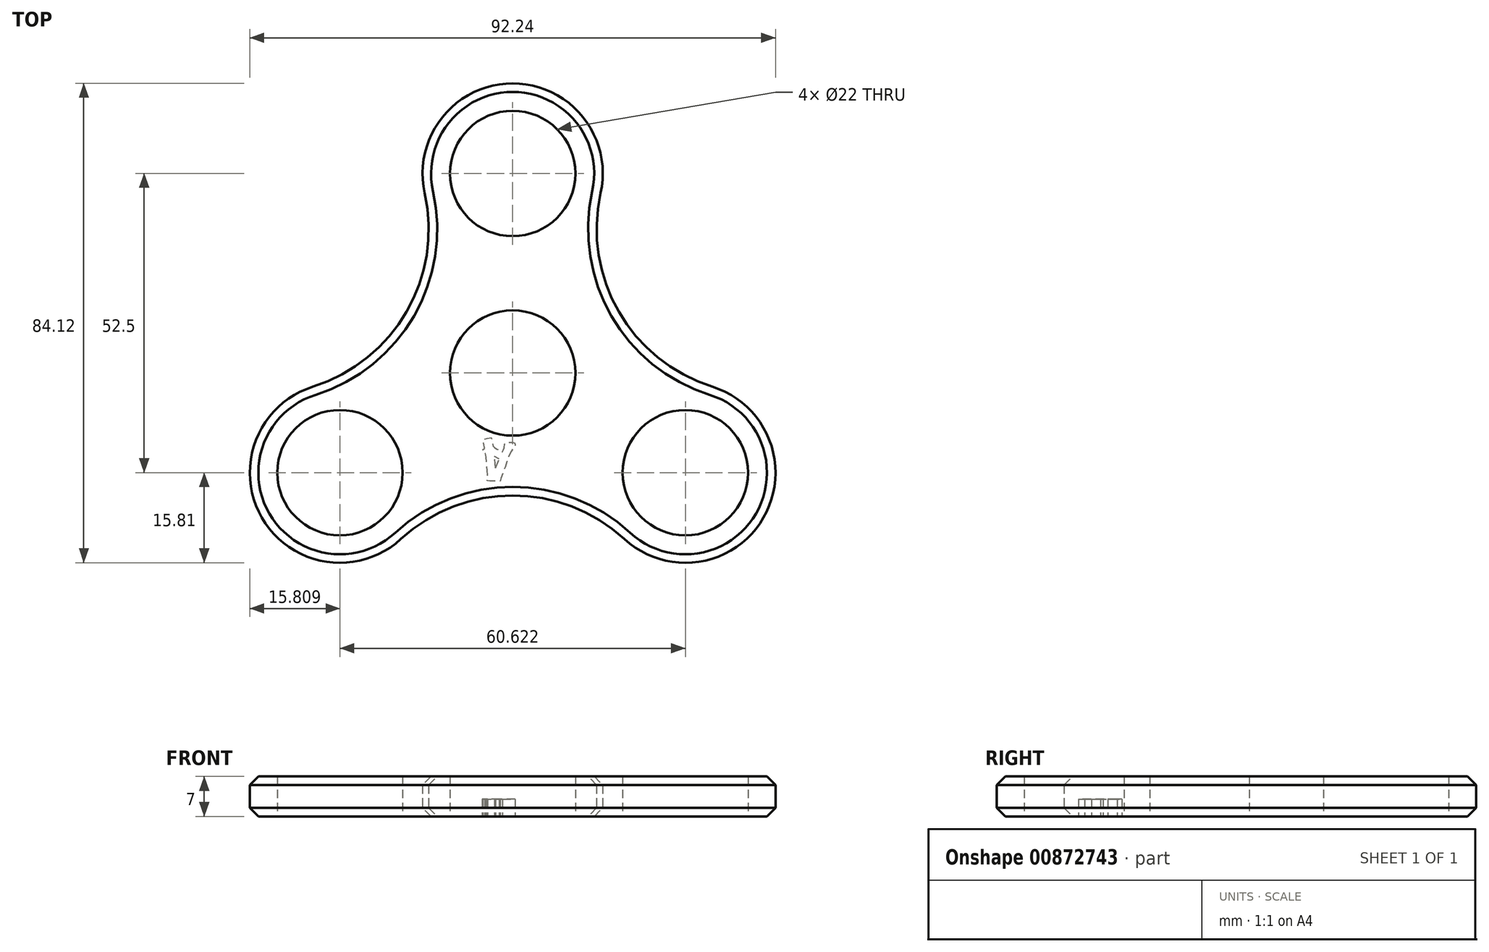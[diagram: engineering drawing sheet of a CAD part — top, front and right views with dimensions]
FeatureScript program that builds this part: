
annotation { "Feature Type Name" : "Feature", "Feature Type Description" : "" }
export const myFeature = defineFeature(function(context is Context, id is Id, definition is map)
    precondition{}
    {
        {
            var Q0;
            Q0=qCreatedBy(makeId("Top.planeOp"),FACE);
            var sketch = newSketch(context, id + "F0", { "sketchPlane" : qUnion([Q0])});
            skCircle(sketch, "E0", {"center": v(0, 0) * mm, "radius": 11 * mm});
            skLineSegment(sketch, "E1", {"start": v(0, 0) * mm, "end": v(0, 35) * mm, "construction": true});
            skArc(sketch, "E2", {"start": v(15.43, 31.56) * mm, "mid": v(0, 50.81) * mm, "end": v(-15.43, 31.56) * mm});
            skArc(sketch, "E3.1.0", {"start": v(-35.04, -2.41) * mm, "mid": v(-44, -25.4) * mm, "end": v(-19.61, -29.14) * mm});
            skArc(sketch, "E3.2.0", {"start": v(19.61, -29.14) * mm, "mid": v(44, -25.4) * mm, "end": v(35.04, -2.41) * mm});
            skArc(sketch, "E4", {"start": v(0, -21.5) * mm, "mid": v(-10.52, -23.48) * mm, "end": v(-19.61, -29.14) * mm});
            skArc(sketch, "E5", {"start": v(19.61, -29.14) * mm, "mid": v(10.52, -23.48) * mm, "end": v(0, -21.5) * mm});
            skArc(sketch, "E6.1.0", {"start": v(18.62, 10.75) * mm, "mid": v(25.6, 2.62) * mm, "end": v(35.04, -2.41) * mm});
            skArc(sketch, "E6.1.1", {"start": v(15.43, 31.56) * mm, "mid": v(15.07, 20.85) * mm, "end": v(18.62, 10.75) * mm});
            skArc(sketch, "E6.2.0", {"start": v(-18.62, 10.75) * mm, "mid": v(-15.07, 20.85) * mm, "end": v(-15.43, 31.56) * mm});
            skArc(sketch, "E6.2.1", {"start": v(-35.04, -2.41) * mm, "mid": v(-25.6, 2.62) * mm, "end": v(-18.62, 10.75) * mm});
            skCircle(sketch, "E7", {"center": v(0, 35) * mm, "radius": 11 * mm});
            skCircle(sketch, "E8.1.0", {"center": v(-30.31, -17.5) * mm, "radius": 11 * mm});
            skCircle(sketch, "E8.2.0", {"center": v(30.31, -17.5) * mm, "radius": 11 * mm});
            skCircle(sketch, "E9.cCircle", {"center": v(0, 17.5) * mm, "radius": 4.9 * mm, "construction": true});
            skLineSegment(sketch, "E9.0", {"start": v(2.83, 22.4) * mm, "end": v(5.66, 17.5) * mm});
            skLineSegment(sketch, "E9.1", {"start": v(5.66, 17.5) * mm, "end": v(2.83, 12.6) * mm});
            skLineSegment(sketch, "E9.2", {"start": v(2.83, 12.6) * mm, "end": v(-2.83, 12.6) * mm});
            skLineSegment(sketch, "E9.3", {"start": v(-2.83, 12.6) * mm, "end": v(-5.66, 17.5) * mm});
            skLineSegment(sketch, "E9.4", {"start": v(-5.66, 17.5) * mm, "end": v(-2.83, 22.4) * mm});
            skLineSegment(sketch, "E9.5", {"start": v(-2.83, 22.4) * mm, "end": v(2.83, 22.4) * mm});
            skLineSegment(sketch, "E10.1.0", {"start": v(-9.5, -8.75) * mm, "end": v(-12.33, -13.65) * mm});
            skLineSegment(sketch, "E10.1.1", {"start": v(-12.33, -13.65) * mm, "end": v(-17.98, -13.65) * mm});
            skLineSegment(sketch, "E10.1.2", {"start": v(-17.98, -13.65) * mm, "end": v(-20.81, -8.75) * mm});
            skLineSegment(sketch, "E10.1.3", {"start": v(-20.81, -8.75) * mm, "end": v(-17.98, -3.85) * mm});
            skLineSegment(sketch, "E10.1.4", {"start": v(-17.98, -3.85) * mm, "end": v(-12.33, -3.85) * mm});
            skLineSegment(sketch, "E10.1.5", {"start": v(-12.33, -3.85) * mm, "end": v(-9.5, -8.75) * mm});
            skLineSegment(sketch, "E10.2.0", {"start": v(12.33, -3.85) * mm, "end": v(17.98, -3.85) * mm});
            skLineSegment(sketch, "E10.2.1", {"start": v(17.98, -3.85) * mm, "end": v(20.81, -8.75) * mm});
            skLineSegment(sketch, "E10.2.2", {"start": v(20.81, -8.75) * mm, "end": v(17.98, -13.65) * mm});
            skLineSegment(sketch, "E10.2.3", {"start": v(17.98, -13.65) * mm, "end": v(12.33, -13.65) * mm});
            skLineSegment(sketch, "E10.2.4", {"start": v(12.33, -13.65) * mm, "end": v(9.5, -8.75) * mm});
            skLineSegment(sketch, "E10.2.5", {"start": v(9.5, -8.75) * mm, "end": v(12.33, -3.85) * mm});
            skLineSegment(sketch, "E11", {"start": v(0, 0) * mm, "end": v(-18.62, 10.75) * mm, "construction": true});
            skCircle(sketch, "E12.cCircle", {"center": v(-14.07, 8.13) * mm, "radius": 4 * mm, "construction": true});
            skLineSegment(sketch, "E12.0", {"start": v(-11.76, 12.13) * mm, "end": v(-9.45, 8.13) * mm});
            skLineSegment(sketch, "E12.1", {"start": v(-9.45, 8.13) * mm, "end": v(-11.76, 4.13) * mm});
            skLineSegment(sketch, "E12.2", {"start": v(-11.76, 4.13) * mm, "end": v(-16.38, 4.13) * mm});
            skLineSegment(sketch, "E12.3", {"start": v(-16.38, 4.13) * mm, "end": v(-18.7, 8.13) * mm});
            skLineSegment(sketch, "E12.4", {"start": v(-18.7, 8.12) * mm, "end": v(-16.38, 12.13) * mm});
            skLineSegment(sketch, "E12.5", {"start": v(-16.38, 12.13) * mm, "end": v(-11.76, 12.13) * mm});
            skPoint(sketch, "E12.0.midPoint", {"position": v(-10.6, 10.13) * mm});
            skLineSegment(sketch, "E13.1.0", {"start": v(2.3, -20.25) * mm, "end": v(-2.3, -20.25) * mm});
            skLineSegment(sketch, "E13.1.1", {"start": v(-2.3, -20.25) * mm, "end": v(-4.62, -16.25) * mm});
            skLineSegment(sketch, "E13.1.2", {"start": v(-4.62, -16.25) * mm, "end": v(-2.3, -12.25) * mm});
            skLineSegment(sketch, "E13.1.3", {"start": v(-2.3, -12.25) * mm, "end": v(2.3, -12.25) * mm});
            skLineSegment(sketch, "E13.1.4", {"start": v(2.3, -12.25) * mm, "end": v(4.62, -16.25) * mm});
            skLineSegment(sketch, "E13.1.5", {"start": v(4.62, -16.25) * mm, "end": v(2.3, -20.25) * mm});
            skLineSegment(sketch, "E13.2.0", {"start": v(16.38, 12.12) * mm, "end": v(18.7, 8.12) * mm});
            skLineSegment(sketch, "E13.2.1", {"start": v(18.7, 8.12) * mm, "end": v(16.38, 4.12) * mm});
            skLineSegment(sketch, "E13.2.2", {"start": v(16.38, 4.12) * mm, "end": v(11.76, 4.12) * mm});
            skLineSegment(sketch, "E13.2.3", {"start": v(11.76, 4.12) * mm, "end": v(9.45, 8.12) * mm});
            skLineSegment(sketch, "E13.2.4", {"start": v(9.45, 8.12) * mm, "end": v(11.76, 12.12) * mm});
            skLineSegment(sketch, "E13.2.5", {"start": v(11.76, 12.12) * mm, "end": v(16.38, 12.12) * mm});
            skSolve(sketch);
        }
        {
            var Q0;
            Q0=makeQuery(id+"F0.imprint","IMPRINT",FACE,{"disambiguationData":[TD([[makeQuery(id+"F0.imprint","IMPRINT",EDGE,{"derivedFrom":sQuery(id+"F0.wireOp",EDGE,"E3.1.0")}),1.0]])]});
            var Q1;
            Q1=makeQuery(id+"F0.imprint","IMPRINT",FACE,{"disambiguationData":[TD([[makeQuery(id+"F0.imprint","IMPRINT",EDGE,{"derivedFrom":sQuery(id+"F0.wireOp",EDGE,"E2")}),1.0]])]});
            var Q2;
            Q2=makeQuery(id+"F0.imprint","IMPRINT",FACE,{"disambiguationData":[TD([[makeQuery(id+"F0.imprint","IMPRINT",EDGE,{"derivedFrom":sQuery(id+"F0.wireOp",EDGE,"E3.2.0")}),1.0]])]});
            var Q3;
            Q3=makeQuery(id+"F0.imprint","IMPRINT",FACE,{"disambiguationData":[TD([[makeQuery(id+"F0.imprint","IMPRINT",EDGE,{"derivedFrom":sQuery(id+"F0.wireOp",EDGE,"E0")}),-1.0]])]});
            var Q4;
            Q4=makeQuery(id+"F0.imprint","IMPRINT",FACE,{"disambiguationData":[TD([[makeQuery(id+"F0.imprint","IMPRINT",EDGE,{"derivedFrom":sQuery(id+"F0.wireOp",EDGE,"E9.0")}),-1.0]])]});
            var Q5;
            Q5=makeQuery(id+"F0.imprint","IMPRINT",FACE,{"disambiguationData":[TD([[makeQuery(id+"F0.imprint","IMPRINT",EDGE,{"derivedFrom":sQuery(id+"F0.wireOp",EDGE,"E10.1.0")}),-1.0]])]});
            var Q6;
            Q6=makeQuery(id+"F0.imprint","IMPRINT",FACE,{"disambiguationData":[TD([[makeQuery(id+"F0.imprint","IMPRINT",EDGE,{"derivedFrom":sQuery(id+"F0.wireOp",EDGE,"E10.2.0")}),-1.0]])]});
            var Q7;
            Q7=makeQuery(id+"F0.imprint","IMPRINT",FACE,{"disambiguationData":[TD([[makeQuery(id+"F0.imprint","IMPRINT",EDGE,{"derivedFrom":sQuery(id+"F0.wireOp",EDGE,"E13.2.0")}),-1.0]])]});
            var Q8;
            Q8=makeQuery(id+"F0.imprint","IMPRINT",FACE,{"disambiguationData":[TD([[makeQuery(id+"F0.imprint","IMPRINT",EDGE,{"derivedFrom":sQuery(id+"F0.wireOp",EDGE,"E13.1.0")}),-1.0]])]});
            var Q9;
            Q9=makeQuery(id+"F0.imprint","IMPRINT",FACE,{"disambiguationData":[TD([[makeQuery(id+"F0.imprint","IMPRINT",EDGE,{"derivedFrom":sQuery(id+"F0.wireOp",EDGE,"E12.0")}),-1.0]])]});
            extrude(context, id + "F1", {"entities" : qUnion([Q0, Q1, Q2, Q3, Q4, Q5, Q6, Q7, Q8, Q9]), "depth" : 7 * mm, "offsetDistance" : 25 * mm});
        }
        {
            var Q0;
            Q0=makeQuery(id+"F1.opExtrude","CAP_EDGE",EDGE,{"disambiguationData":[OSD([sQuery(id+"F0.wireOp",EDGE,"E6.2.1")])],"isStart":true});
            var Q1;
            Q1=makeQuery(id+"F1.opExtrude","CAP_EDGE",EDGE,{"disambiguationData":[OSD([sQuery(id+"F0.wireOp",EDGE,"E6.2.0")])],"isStart":true});
            var Q2;
            Q2=makeQuery(id+"F1.opExtrude","CAP_EDGE",EDGE,{"disambiguationData":[OSD([sQuery(id+"F0.wireOp",EDGE,"E2")])],"isStart":true});
            var Q3;
            Q3=makeQuery(id+"F1.opExtrude","CAP_EDGE",EDGE,{"disambiguationData":[OSD([sQuery(id+"F0.wireOp",EDGE,"E6.1.1")])],"isStart":true});
            var Q4;
            Q4=makeQuery(id+"F1.opExtrude","CAP_EDGE",EDGE,{"disambiguationData":[OSD([sQuery(id+"F0.wireOp",EDGE,"E6.1.0")])],"isStart":true});
            var Q5;
            Q5=makeQuery(id+"F1.opExtrude","CAP_EDGE",EDGE,{"disambiguationData":[OSD([sQuery(id+"F0.wireOp",EDGE,"E3.2.0")])],"isStart":true});
            var Q6;
            Q6=makeQuery(id+"F1.opExtrude","CAP_EDGE",EDGE,{"disambiguationData":[OSD([sQuery(id+"F0.wireOp",EDGE,"E5")])],"isStart":true});
            var Q7;
            Q7=makeQuery(id+"F1.opExtrude","CAP_EDGE",EDGE,{"disambiguationData":[OSD([sQuery(id+"F0.wireOp",EDGE,"E4")])],"isStart":true});
            var Q8;
            Q8=makeQuery(id+"F1.opExtrude","CAP_EDGE",EDGE,{"disambiguationData":[OSD([sQuery(id+"F0.wireOp",EDGE,"E3.1.0")])],"isStart":true});
            var Q9;
            Q9=makeQuery(id+"F1.opExtrude","CAP_EDGE",EDGE,{"disambiguationData":[OSD([sQuery(id+"F0.wireOp",EDGE,"E2")])],"isStart":false});
            var Q10;
            Q10=makeQuery(id+"F1.opExtrude","CAP_EDGE",EDGE,{"disambiguationData":[OSD([sQuery(id+"F0.wireOp",EDGE,"E6.2.0")])],"isStart":false});
            var Q11;
            Q11=makeQuery(id+"F1.opExtrude","CAP_EDGE",EDGE,{"disambiguationData":[OSD([sQuery(id+"F0.wireOp",EDGE,"E6.2.1")])],"isStart":false});
            var Q12;
            Q12=makeQuery(id+"F1.opExtrude","CAP_EDGE",EDGE,{"disambiguationData":[OSD([sQuery(id+"F0.wireOp",EDGE,"E3.1.0")])],"isStart":false});
            var Q13;
            Q13=makeQuery(id+"F1.opExtrude","CAP_EDGE",EDGE,{"disambiguationData":[OSD([sQuery(id+"F0.wireOp",EDGE,"E5")])],"isStart":false});
            var Q14;
            Q14=makeQuery(id+"F1.opExtrude","CAP_EDGE",EDGE,{"disambiguationData":[OSD([sQuery(id+"F0.wireOp",EDGE,"E4")])],"isStart":false});
            var Q15;
            Q15=makeQuery(id+"F1.opExtrude","CAP_EDGE",EDGE,{"disambiguationData":[OSD([sQuery(id+"F0.wireOp",EDGE,"E3.2.0")])],"isStart":false});
            var Q16;
            Q16=makeQuery(id+"F1.opExtrude","CAP_EDGE",EDGE,{"disambiguationData":[OSD([sQuery(id+"F0.wireOp",EDGE,"E6.1.0")])],"isStart":false});
            var Q17;
            Q17=makeQuery(id+"F1.opExtrude","CAP_EDGE",EDGE,{"disambiguationData":[OSD([sQuery(id+"F0.wireOp",EDGE,"E6.1.1")])],"isStart":false});
            chamfer(context, id + "F2", {"entities" : qUnion([Q0, Q1, Q2, Q3, Q4, Q5, Q6, Q7, Q8, Q9, Q10, Q11, Q12, Q13, Q14, Q15, Q16, Q17]), "width" : 1.5 * mm, "tangentPropagation" : true});
        }
        {
            var Q0;
            Q0=makeQuery(id+"F1.opExtrude","CAP_FACE",FACE,{"disambiguationData":[OSD([sQuery(id+"F0.wireOp",EDGE,"E0"),sQuery(id+"F0.wireOp",EDGE,"E2"),sQuery(id+"F0.wireOp",EDGE,"E3.1.0"),sQuery(id+"F0.wireOp",EDGE,"E3.2.0"),sQuery(id+"F0.wireOp",EDGE,"E4"),sQuery(id+"F0.wireOp",EDGE,"E5"),sQuery(id+"F0.wireOp",EDGE,"E6.1.0"),sQuery(id+"F0.wireOp",EDGE,"E6.1.1"),sQuery(id+"F0.wireOp",EDGE,"E6.2.0"),sQuery(id+"F0.wireOp",EDGE,"E6.2.1"),sQuery(id+"F0.wireOp",EDGE,"E7"),sQuery(id+"F0.wireOp",EDGE,"E8.1.0"),sQuery(id+"F0.wireOp",EDGE,"E8.2.0")])],"isStart":true});
            var sketch = newSketch(context, id + "F3", { "sketchPlane" : qUnion([Q0])});
            skFitSpline(sketch, "E14", {"points": [v(15.47, 11.75) * mm, v(15.3, 11.71) * mm, v(15.13, 11.7) * mm, v(15, 11.62) * mm, v(13.64, 10.78) * mm, v(12.3, 9.92) * mm, v(10.95, 9.1) * mm, v(10.42, 8.77) * mm, v(9.83, 8.53) * mm, v(9.28, 8.23) * mm, v(9.17, 8.16) * mm, v(9.04, 7.95) * mm, v(9.07, 7.84) * mm, v(9.18, 7.4) * mm, v(9.3, 6.95) * mm, v(9.49, 6.52) * mm, v(9.64, 6.17) * mm, v(9.9, 6.15) * mm, v(10.2, 6.42) * mm, v(10.32, 6.55) * mm, v(10.4, 6.74) * mm, v(10.54, 6.83) * mm, v(11.24, 7.29) * mm, v(11.96, 7.72) * mm, v(12.67, 8.16) * mm]});
            skFitSpline(sketch, "E15", {"points": [v(12.67, 8.16) * mm, v(12.69, 8.14) * mm, v(12.7, 8.13) * mm, v(12.72, 8.11) * mm]});
            skFitSpline(sketch, "E16", {"points": [v(12.72, 8.11) * mm, v(12.74, 8.1) * mm, v(12.76, 8.08) * mm, v(12.77, 8.07) * mm]});
            skFitSpline(sketch, "E17", {"points": [v(12.77, 8.07) * mm, v(12.12, 7.22) * mm, v(11.46, 6.37) * mm, v(10.81, 5.52) * mm, v(10.72, 5.4) * mm, v(10.56, 5.22) * mm, v(10.6, 5.12) * mm, v(10.78, 4.55) * mm, v(11, 3.98) * mm, v(11.25, 3.45) * mm, v(11.4, 3.15) * mm, v(11.67, 3.2) * mm, v(11.94, 3.36) * mm, v(13.17, 4.15) * mm, v(14.4, 4.95) * mm, v(15.65, 5.71) * mm]});
            skFitSpline(sketch, "E18", {"points": [v(15.65, 5.71) * mm, v(16.44, 6.2) * mm, v(17.26, 6.62) * mm, v(18.06, 7.09) * mm, v(18.15, 7.14) * mm, v(18.24, 7.35) * mm, v(18.2, 7.43) * mm, v(18.05, 7.81) * mm, v(17.88, 8.2) * mm, v(17.65, 8.55) * mm, v(17.47, 8.8) * mm, v(17.24, 8.78) * mm, v(16.93, 8.57) * mm, v(15.92, 7.88) * mm, v(14.86, 7.24) * mm, v(13.82, 6.58) * mm]});
            skFitSpline(sketch, "E19", {"points": [v(13.82, 6.58) * mm, v(13.8, 6.62) * mm, v(13.76, 6.65) * mm, v(13.74, 6.68) * mm]});
            skFitSpline(sketch, "E20", {"points": [v(13.74, 6.68) * mm, v(14.3, 7.34) * mm, v(14.88, 7.98) * mm, v(15.42, 8.65) * mm, v(16.46, 9.95) * mm, v(16.63, 9.94) * mm, v(15.81, 11.51) * mm]});
            skFitSpline(sketch, "E21", {"points": [v(2.9, -16.8) * mm, v(2.9, -17.17) * mm, v(2.9, -17.54) * mm, v(2.88, -17.92) * mm, v(2.85, -18.56) * mm, v(2.85, -18.57) * mm, v(3.5, -18.75) * mm, v(3.56, -18.76) * mm, v(3.63, -18.78) * mm, v(3.7, -18.8) * mm]});
            skFitSpline(sketch, "E22", {"points": [v(3.7, -18.8) * mm, v(4.31, -18.92) * mm, v(4.61, -18.66) * mm, v(4.54, -18.03) * mm, v(4.32, -16.04) * mm, v(4.08, -14.05) * mm, v(3.87, -12.06) * mm, v(3.83, -11.63) * mm, v(3.62, -11.46) * mm, v(3.25, -11.4) * mm, v(3.07, -11.36) * mm, v(2.89, -11.35) * mm, v(2.7, -11.36) * mm, v(2.21, -11.38) * mm, v(2.12, -11.58) * mm, v(2.25, -12.06) * mm, v(2.4, -12.6) * mm, v(2.46, -13.17) * mm, v(2.56, -13.73) * mm]});
            skFitSpline(sketch, "E23", {"points": [v(-1.83, 13.85) * mm, v(-1.7, 13.54) * mm, v(-1.55, 13.34) * mm, v(-1.5, 13.1) * mm, v(-1.36, 12.35) * mm, v(-0.84, 12.16) * mm, v(-0.17, 12.18) * mm, v(0.01, 12.19) * mm, v(0.34, 12.2) * mm, v(0.36, 12.29) * mm, v(0.42, 12.5) * mm, v(0.41, 12.78) * mm, v(0.3, 12.96) * mm, v(-0.6, 14.43) * mm, v(-1.17, 16.03) * mm, v(-1.73, 17.64) * mm, v(-2.2, 18.99) * mm, v(-2.19, 19) * mm, v(-3.64, 18.99) * mm, v(-3.8, 18.99) * mm, v(-3.95, 18.97) * mm, v(-4.1, 18.96) * mm, v(-4.42, 18.94) * mm, v(-4.52, 18.8) * mm, v(-4.44, 18.49) * mm, v(-4.39, 18.3) * mm, v(-4.4, 18.1) * mm, v(-4.4, 17.9) * mm]});
            skFitSpline(sketch, "E24", {"points": [v(-4.4, 17.9) * mm, v(-4.5, 16.76) * mm, v(-4.61, 15.63) * mm, v(-4.72, 14.5) * mm, v(-4.73, 14.38) * mm, v(-4.72, 14.23) * mm, v(-4.8, 14.17) * mm, v(-5.11, 13.89) * mm, v(-5.36, 13.61) * mm, v(-4.97, 13.2) * mm, v(-4.93, 13.16) * mm, v(-4.97, 13.03) * mm, v(-4.99, 12.95) * mm, v(-5.03, 12.7) * mm, v(-5.06, 12.45) * mm, v(-5.13, 12.2) * mm, v(-5.24, 11.82) * mm, v(-5.1, 11.65) * mm, v(-4.72, 11.56) * mm, v(-3.74, 11.33) * mm, v(-3.74, 11.33) * mm, v(-3.55, 12.29) * mm, v(-3.5, 12.56) * mm, v(-3.42, 12.9) * mm, v(-3.23, 13.06) * mm, v(-2.82, 13.37) * mm, v(-2.34, 13.57) * mm, v(-1.83, 13.85) * mm]});
            skFitSpline(sketch, "E25", {"points": [v(-16.86, 2.82) * mm, v(-16.78, 2.83) * mm, v(-16.72, 2.84) * mm, v(-16.67, 2.83) * mm, v(-15.35, 2.72) * mm, v(-14.03, 2.6) * mm, v(-12.71, 2.47) * mm, v(-12.55, 2.45) * mm, v(-12.39, 2.39) * mm, v(-12.24, 2.3) * mm, v(-11.98, 2.17) * mm, v(-11.8, 2.23) * mm, v(-11.7, 2.5) * mm, v(-11.57, 2.82) * mm, v(-11.48, 3.16) * mm, v(-11.37, 3.5) * mm, v(-11.25, 3.84) * mm, v(-11.42, 4.02) * mm, v(-11.74, 4.04) * mm, v(-12, 4.07) * mm, v(-12.27, 4) * mm, v(-12.53, 4.02) * mm, v(-13.98, 4.14) * mm, v(-15.42, 4.27) * mm, v(-16.87, 4.41) * mm, v(-16.97, 4.42) * mm, v(-17.13, 4.52) * mm, v(-17.14, 4.59) * mm, v(-17.18, 4.93) * mm, v(-17.22, 5.28) * mm, v(-17.18, 5.61) * mm]});
            skFitSpline(sketch, "E26", {"points": [v(-17.18, 5.61) * mm, v(-17.15, 5.93) * mm, v(-17.2, 6.12) * mm, v(-17.55, 6.12) * mm, v(-17.83, 6.12) * mm, v(-18.1, 6.1) * mm, v(-18.38, 6.05) * mm]});
            skFitSpline(sketch, "E27", {"points": [v(-18.38, 6.05) * mm, v(-18.73, 5.99) * mm, v(-18.83, 5.75) * mm, v(-18.77, 5.42) * mm, v(-18.68, 4.97) * mm, v(-18.58, 4.51) * mm, v(-18.5, 4.05) * mm, v(-18.4, 3.36) * mm, v(-18.3, 2.66) * mm, v(-18.18, 1.96) * mm, v(-18.14, 1.7) * mm, v(-18.06, 1.45) * mm, v(-18, 1.19) * mm]});
            skFitSpline(sketch, "E28", {"points": [v(-18, 1.19) * mm, v(-17.75, 1.26) * mm, v(-17.5, 1.33) * mm, v(-17.26, 1.41) * mm, v(-17.2, 1.43) * mm, v(-17.16, 1.47) * mm, v(-17.12, 1.5) * mm, v(-16.8, 1.69) * mm, v(-16.59, 1.9) * mm, v(-16.8, 2.32) * mm, v(-16.86, 2.46) * mm, v(-16.84, 2.64) * mm, v(-16.86, 2.82) * mm]});
            skFitSpline(sketch, "E29", {"points": [v(11.05, -4.16) * mm, v(11.05, -4.16) * mm, v(11.04, -4.16) * mm, v(11.04, -4.16) * mm]});
            skFitSpline(sketch, "E30", {"points": [v(11.04, -4.16) * mm, v(11.01, -4.2) * mm, v(10.98, -4.25) * mm, v(10.95, -4.3) * mm, v(10.57, -4.86) * mm, v(10.68, -5.06) * mm, v(11.38, -5.14) * mm, v(11.54, -5.16) * mm, v(11.7, -5.2) * mm, v(11.86, -5.26) * mm, v(13, -5.66) * mm, v(14.15, -6.05) * mm, v(15.28, -6.48) * mm, v(15.95, -6.73) * mm, v(16.58, -7.06) * mm, v(17.23, -7.34) * mm]});
            skFitSpline(sketch, "E31", {"points": [v(17.23, -7.34) * mm, v(17.34, -7.38) * mm, v(17.57, -7.36) * mm, v(17.6, -7.3) * mm, v(17.83, -6.91) * mm, v(18.03, -6.51) * mm, v(18.2, -6.1) * mm, v(18.22, -6.03) * mm, v(18.04, -5.82) * mm, v(17.92, -5.77) * mm, v(15.9, -5.04) * mm, v(13.88, -4.32) * mm, v(11.85, -3.62) * mm, v(11.71, -3.57) * mm, v(11.5, -3.63) * mm, v(11.37, -3.72) * mm, v(11.23, -3.82) * mm, v(11.15, -4) * mm, v(11.05, -4.16) * mm]});
            skFitSpline(sketch, "E32", {"points": [v(-15.12, -11.88) * mm, v(-14.92, -11.83) * mm, v(-14.74, -11.83) * mm, v(-14.62, -11.75) * mm, v(-12.97, -10.53) * mm, v(-11.33, -9.3) * mm, v(-9.67, -8.09) * mm, v(-9.15, -7.7) * mm, v(-9.12, -7.69) * mm, v(-9.36, -7.08) * mm]});
            skFitSpline(sketch, "E33", {"points": [v(-9.36, -7.08) * mm, v(-9.4, -6.96) * mm, v(-9.45, -6.84) * mm, v(-9.5, -6.73) * mm]});
            skFitSpline(sketch, "E34", {"points": [v(-9.5, -6.73) * mm, v(-9.73, -6.24) * mm, v(-10.02, -6.2) * mm, v(-10.37, -6.63) * mm]});
            skFitSpline(sketch, "E35", {"points": [v(-10.37, -6.63) * mm, v(-10.49, -6.77) * mm, v(-10.62, -6.9) * mm, v(-10.76, -7) * mm, v(-11.5, -7.55) * mm, v(-12.22, -8.1) * mm, v(-12.97, -8.62) * mm, v(-13.8, -9.2) * mm, v(-14.68, -9.74) * mm, v(-15.52, -10.32) * mm, v(-15.62, -10.38) * mm, v(-15.72, -10.59) * mm, v(-15.7, -10.68) * mm, v(-15.54, -11.07) * mm, v(-15.34, -11.43) * mm, v(-15.12, -11.88) * mm]});
            skFitSpline(sketch, "E36", {"points": [v(15.81, 11.51) * mm, v(16.63, 9.94) * mm, v(16.46, 9.95) * mm, v(15.42, 8.65) * mm, v(14.88, 7.98) * mm, v(14.3, 7.34) * mm, v(13.74, 6.68) * mm]});
            skFitSpline(sketch, "E37", {"points": [v(13.74, 6.68) * mm, v(13.76, 6.65) * mm, v(13.8, 6.62) * mm, v(13.82, 6.58) * mm]});
            skFitSpline(sketch, "E38", {"points": [v(13.82, 6.58) * mm, v(14.86, 7.24) * mm, v(15.92, 7.88) * mm, v(16.93, 8.57) * mm, v(17.24, 8.78) * mm, v(17.47, 8.8) * mm, v(17.65, 8.55) * mm, v(17.88, 8.2) * mm, v(18.05, 7.81) * mm, v(18.2, 7.43) * mm, v(18.24, 7.35) * mm, v(18.15, 7.14) * mm, v(18.06, 7.09) * mm, v(17.26, 6.62) * mm, v(16.44, 6.2) * mm, v(15.65, 5.71) * mm]});
            skFitSpline(sketch, "E39", {"points": [v(15.65, 5.71) * mm, v(14.4, 4.95) * mm, v(13.17, 4.15) * mm, v(11.94, 3.36) * mm, v(11.67, 3.2) * mm, v(11.4, 3.15) * mm, v(11.25, 3.45) * mm, v(11, 3.98) * mm, v(10.78, 4.55) * mm, v(10.6, 5.12) * mm, v(10.58, 5.17) * mm, v(10.6, 5.24) * mm, v(10.65, 5.3) * mm]});
            skFitSpline(sketch, "E40", {"points": [v(10.65, 5.3) * mm, v(10.7, 5.38) * mm, v(10.76, 5.46) * mm, v(10.81, 5.52) * mm, v(11.46, 6.37) * mm, v(12.12, 7.22) * mm, v(12.77, 8.07) * mm]});
            skFitSpline(sketch, "E41", {"points": [v(12.77, 8.07) * mm, v(12.74, 8.1) * mm, v(12.7, 8.13) * mm, v(12.67, 8.16) * mm]});
            skFitSpline(sketch, "E42", {"points": [v(12.67, 8.16) * mm, v(11.96, 7.72) * mm, v(11.24, 7.29) * mm, v(10.54, 6.83) * mm, v(10.4, 6.74) * mm, v(10.32, 6.55) * mm, v(10.2, 6.42) * mm, v(9.9, 6.15) * mm, v(9.64, 6.17) * mm, v(9.49, 6.52) * mm, v(9.3, 6.95) * mm, v(9.18, 7.4) * mm, v(9.07, 7.84) * mm, v(9.04, 7.95) * mm, v(9.17, 8.16) * mm, v(9.28, 8.23) * mm, v(9.83, 8.53) * mm, v(10.42, 8.77) * mm, v(10.95, 9.1) * mm, v(12.3, 9.92) * mm, v(13.64, 10.78) * mm, v(15, 11.62) * mm, v(15.13, 11.7) * mm, v(15.3, 11.71) * mm, v(15.47, 11.75) * mm]});
            skFitSpline(sketch, "E43", {"points": [v(15.47, 11.75) * mm, v(15.58, 11.67) * mm, v(15.7, 11.6) * mm, v(15.81, 11.51) * mm]});
            skFitSpline(sketch, "E44", {"points": [v(2.9, -16.8) * mm, v(2.54, -17.5) * mm, v(2.18, -18.21) * mm, v(1.82, -18.92) * mm, v(1.6, -19.35) * mm, v(1.46, -19.4) * mm, v(1.02, -19.24) * mm, v(0.93, -19.2) * mm, v(0.83, -19.17) * mm, v(0.75, -19.12) * mm, v(0.14, -18.8) * mm, v(0.1, -18.63) * mm, v(0.45, -18.04) * mm, v(0.89, -17.29) * mm, v(1.31, -16.52) * mm, v(1.75, -15.77) * mm, v(1.9, -15.5) * mm, v(1.87, -15.32) * mm, v(1.63, -15.12) * mm, v(1.1, -14.67) * mm, v(0.61, -14.2) * mm, v(0.1, -13.73) * mm, v(0.02, -13.65) * mm, v(-0.08, -13.56) * mm, v(-0.18, -13.55) * mm, v(-0.67, -13.5) * mm, v(-0.61, -13.21) * mm, v(-0.5, -12.89) * mm, v(-0.45, -12.74) * mm, v(-0.4, -12.6) * mm, v(-0.34, -12.45) * mm, v(-0.03, -11.73) * mm, v(0.17, -11.68) * mm, v(0.76, -12.2) * mm, v(1, -12.42) * mm, v(1.23, -12.63) * mm, v(1.46, -12.85) * mm]});
            skFitSpline(sketch, "E45", {"points": [v(1.46, -12.85) * mm, v(1.7, -13.06) * mm, v(1.93, -13.28) * mm, v(2.16, -13.49) * mm, v(2.28, -13.6) * mm, v(2.42, -13.69) * mm, v(2.66, -13.75) * mm]});
            skFitSpline(sketch, "E46", {"points": [v(-2.99, 16.66) * mm, v(-3.06, 16.02) * mm, v(-3.13, 15.37) * mm, v(-3.2, 14.67) * mm]});
            skFitSpline(sketch, "E47", {"points": [v(-16.86, 2.82) * mm, v(-16.84, 2.64) * mm, v(-16.86, 2.46) * mm, v(-16.8, 2.32) * mm, v(-16.59, 1.9) * mm, v(-16.8, 1.69) * mm, v(-17.12, 1.5) * mm, v(-17.16, 1.47) * mm, v(-17.2, 1.43) * mm, v(-17.26, 1.41) * mm, v(-17.5, 1.33) * mm, v(-17.75, 1.26) * mm, v(-18, 1.19) * mm]});
            skFitSpline(sketch, "E48", {"points": [v(-18, 1.19) * mm, v(-18.06, 1.45) * mm, v(-18.14, 1.7) * mm, v(-18.18, 1.96) * mm, v(-18.3, 2.66) * mm, v(-18.4, 3.36) * mm, v(-18.5, 4.05) * mm, v(-18.58, 4.51) * mm, v(-18.68, 4.97) * mm, v(-18.77, 5.42) * mm, v(-18.83, 5.75) * mm, v(-18.73, 5.99) * mm, v(-18.38, 6.05) * mm]});
            skFitSpline(sketch, "E49", {"points": [v(-18.38, 6.05) * mm, v(-18.1, 6.1) * mm, v(-17.83, 6.12) * mm, v(-17.55, 6.12) * mm, v(-17.2, 6.12) * mm, v(-17.15, 5.93) * mm, v(-17.18, 5.61) * mm]});
            skFitSpline(sketch, "E50", {"points": [v(-17.18, 5.61) * mm, v(-17.22, 5.28) * mm, v(-17.18, 4.93) * mm, v(-17.14, 4.59) * mm, v(-17.13, 4.52) * mm, v(-16.97, 4.42) * mm, v(-16.87, 4.41) * mm, v(-15.42, 4.27) * mm, v(-13.98, 4.14) * mm, v(-12.53, 4.02) * mm, v(-12.27, 4) * mm, v(-12, 4.07) * mm, v(-11.74, 4.04) * mm, v(-11.42, 4.02) * mm, v(-11.25, 3.84) * mm, v(-11.37, 3.5) * mm, v(-11.48, 3.16) * mm, v(-11.57, 2.82) * mm, v(-11.7, 2.5) * mm, v(-11.8, 2.23) * mm, v(-11.98, 2.17) * mm, v(-12.24, 2.3) * mm, v(-12.39, 2.39) * mm, v(-12.55, 2.45) * mm, v(-12.71, 2.47) * mm, v(-14.03, 2.6) * mm, v(-15.35, 2.72) * mm, v(-16.67, 2.83) * mm, v(-16.72, 2.84) * mm, v(-16.78, 2.83) * mm, v(-16.86, 2.82) * mm]});
            skFitSpline(sketch, "E51", {"points": [v(11.05, -4.16) * mm, v(11.15, -4) * mm, v(11.23, -3.82) * mm, v(11.37, -3.72) * mm, v(11.5, -3.63) * mm, v(11.71, -3.57) * mm, v(11.85, -3.62) * mm, v(13.88, -4.32) * mm, v(15.9, -5.04) * mm, v(17.92, -5.77) * mm, v(18.04, -5.82) * mm, v(18.22, -6.03) * mm, v(18.2, -6.1) * mm, v(18.03, -6.51) * mm, v(17.83, -6.91) * mm, v(17.6, -7.3) * mm, v(17.57, -7.36) * mm, v(17.34, -7.38) * mm, v(17.23, -7.34) * mm]});
            skFitSpline(sketch, "E52", {"points": [v(17.23, -7.34) * mm, v(16.58, -7.06) * mm, v(15.95, -6.73) * mm, v(15.28, -6.48) * mm, v(14.15, -6.05) * mm, v(13, -5.66) * mm, v(11.86, -5.26) * mm, v(11.7, -5.2) * mm, v(11.54, -5.16) * mm, v(11.38, -5.14) * mm, v(10.68, -5.06) * mm, v(10.57, -4.86) * mm, v(10.95, -4.3) * mm, v(10.98, -4.25) * mm, v(11.01, -4.2) * mm, v(11.04, -4.16) * mm]});
            skFitSpline(sketch, "E53", {"points": [v(11.04, -4.16) * mm, v(11.04, -4.16) * mm, v(11.05, -4.16) * mm, v(11.05, -4.16) * mm]});
            skFitSpline(sketch, "E54", {"points": [v(-15.12, -11.88) * mm, v(-15.34, -11.43) * mm, v(-15.54, -11.07) * mm, v(-15.7, -10.68) * mm, v(-15.72, -10.59) * mm, v(-15.62, -10.38) * mm, v(-15.52, -10.32) * mm, v(-14.68, -9.74) * mm, v(-13.8, -9.2) * mm, v(-12.97, -8.62) * mm, v(-12.22, -8.1) * mm, v(-11.5, -7.55) * mm, v(-10.76, -7) * mm, v(-10.62, -6.9) * mm, v(-10.49, -6.77) * mm, v(-10.37, -6.63) * mm]});
            skFitSpline(sketch, "E55", {"points": [v(-10.37, -6.63) * mm, v(-10.02, -6.2) * mm, v(-9.73, -6.24) * mm, v(-9.5, -6.73) * mm]});
            skFitSpline(sketch, "E56", {"points": [v(-9.5, -6.73) * mm, v(-9.45, -6.84) * mm, v(-9.4, -6.96) * mm, v(-9.36, -7.08) * mm]});
            skFitSpline(sketch, "E57", {"points": [v(-9.36, -7.08) * mm, v(-9.12, -7.69) * mm, v(-9.15, -7.7) * mm, v(-9.67, -8.09) * mm, v(-11.33, -9.3) * mm, v(-12.97, -10.53) * mm, v(-14.62, -11.75) * mm, v(-14.74, -11.83) * mm, v(-14.92, -11.83) * mm, v(-15.12, -11.88) * mm]});
            skFitSpline(sketch, "E58", {"points": [v(-2.36, 15.09) * mm, v(-2.63, 14.95) * mm, v(-2.88, 14.83) * mm, v(-3.2, 14.67) * mm]});
            skFitSpline(sketch, "E59", {"points": [v(-2.99, 16.66) * mm, v(-2.79, 16.16) * mm, v(-2.58, 15.65) * mm, v(-2.36, 15.09) * mm]});
            skSolve(sketch);
        }
        {
            var Q0;
            Q0=makeQuery(id+"F3.imprint","IMPRINT",FACE,{"disambiguationData":[TD([[makeQuery(id+"F3.imprint","IMPRINT",EDGE,{"derivedFrom":sQuery(id+"F3.wireOp",EDGE,"E23")}),1.0]])]});
            var Q1;
            Q1=makeQuery(id+"F3.imprint","IMPRINT",FACE,{"disambiguationData":[TD([[makeQuery(id+"F3.imprint","IMPRINT",EDGE,{"derivedFrom":sQuery(id+"F3.wireOp",EDGE,"E47")}),-1.0]])]});
            var Q2;
            Q2=makeQuery(id+"F3.imprint","IMPRINT",FACE,{"disambiguationData":[TD([[makeQuery(id+"F3.imprint","IMPRINT",EDGE,{"derivedFrom":sQuery(id+"F3.wireOp",EDGE,"E54")}),-1.0]])]});
            var Q3;
            Q3=makeQuery(id+"F3.imprint","IMPRINT",FACE,{"disambiguationData":[TD([[makeQuery(id+"F3.imprint","IMPRINT",EDGE,{"derivedFrom":sQuery(id+"F3.wireOp",EDGE,"E51")}),-1.0]])]});
            var Q4;
            Q4=makeQuery(id+"F3.imprint","IMPRINT",FACE,{"disambiguationData":[TD([[makeQuery(id+"F3.imprint","IMPRINT",EDGE,{"derivedFrom":sQuery(id+"F3.wireOp",EDGE,"E36")}),-1.0]])]});
            var Q5;
            Q5=makeQuery(id+"F3.imprint","IMPRINT",FACE,{"disambiguationData":[TD([[makeQuery(id+"F3.imprint","IMPRINT",EDGE,{"derivedFrom":sQuery(id+"F3.wireOp",EDGE,"E21")}),1.0]])]});
            extrude(context, id + "F4", {"entities" : qUnion([Q0, Q1, Q2, Q3, Q4, Q5]), "operationType" : NewBodyOperationType.REMOVE, "oppositeDirection" : true, "depth" : 3 * mm, "offsetDistance" : 25 * mm});
        }
    });
